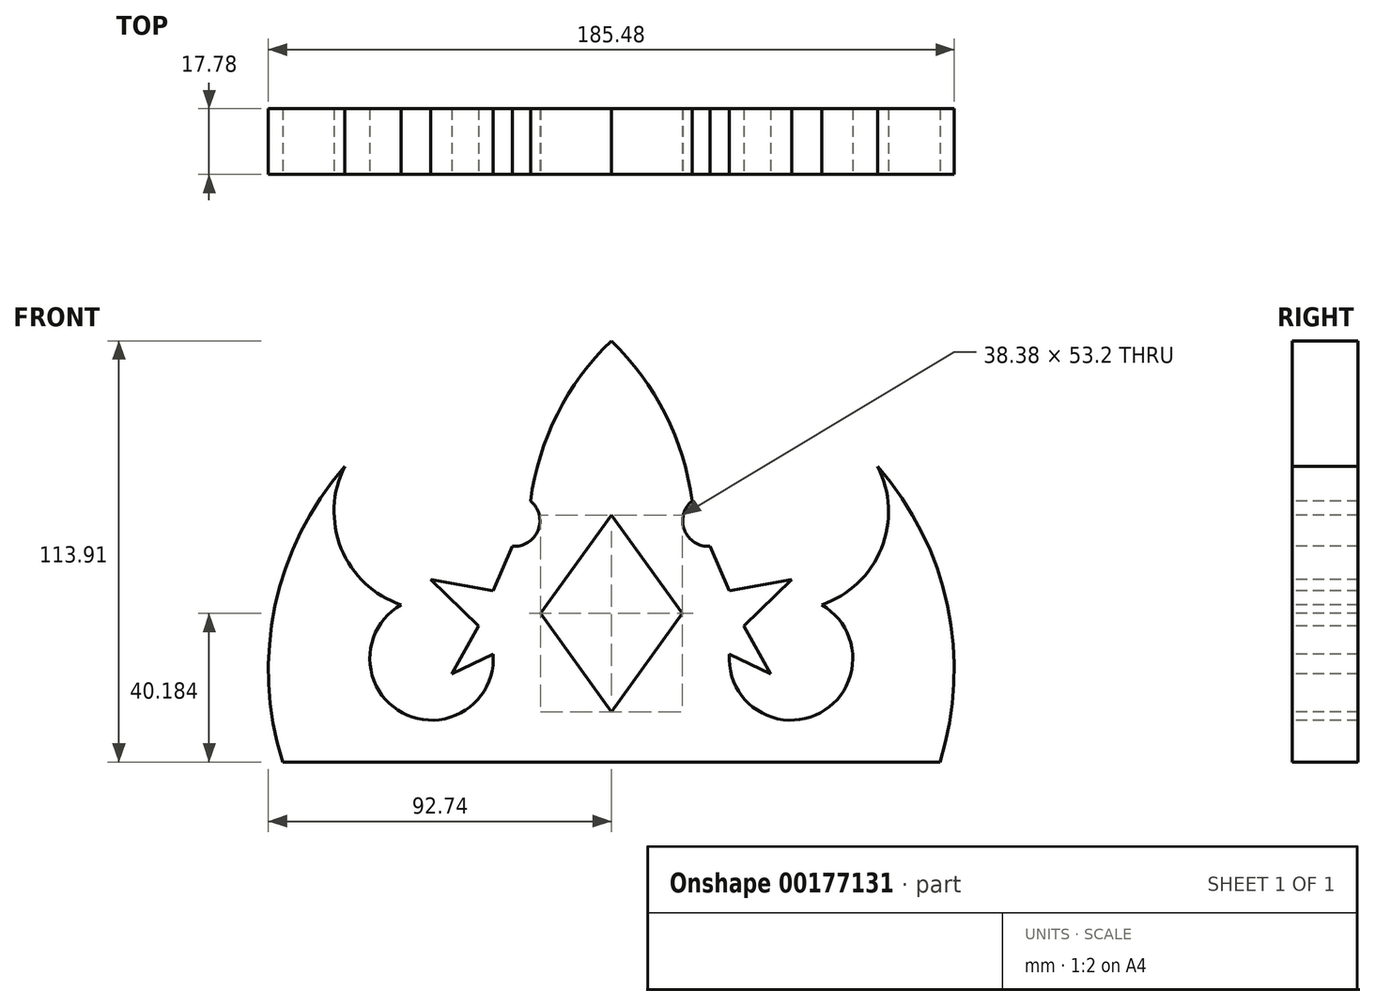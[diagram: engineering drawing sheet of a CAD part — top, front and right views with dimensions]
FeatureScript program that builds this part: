
annotation { "Feature Type Name" : "Feature", "Feature Type Description" : "" }
export const myFeature = defineFeature(function(context is Context, id is Id, definition is map)
    precondition{}
    {
        {
            var Q0;
            Q0=qCreatedBy(makeId("Front.planeOp"),FACE);
            var sketch = newSketch(context, id + "F0", { "sketchPlane" : qUnion([Q0])});
            skLineSegment(sketch, "E0", {"start": v(0, 0) * mm, "end": v(88.9, 0) * mm});
            skLineSegment(sketch, "E1", {"start": v(0, 0) * mm, "end": v(-88.9, 0) * mm});
            skArc(sketch, "E2", {"start": v(-72.07, 79.92) * mm, "mid": v(-90.96, 42.16) * mm, "end": v(-88.9, 0) * mm});
            skArc(sketch, "E3", {"start": v(-72.07, 79.92) * mm, "mid": v(-73.05, 57.73) * mm, "end": v(-56.9, 42.5) * mm});
            skArc(sketch, "E4", {"start": v(-56.9, 42.5) * mm, "mid": v(-56.5, 13.27) * mm, "end": v(-31.93, 29.1) * mm});
            skLineSegment(sketch, "E5", {"start": v(-31.93, 29.1) * mm, "end": v(-43.12, 23.84) * mm});
            skLineSegment(sketch, "E6", {"start": v(-43.12, 23.84) * mm, "end": v(-35.9, 36.76) * mm});
            skLineSegment(sketch, "E7", {"start": v(-35.9, 36.76) * mm, "end": v(-48.82, 49.3) * mm});
            skLineSegment(sketch, "E8", {"start": v(-48.82, 49.3) * mm, "end": v(-31.93, 46.26) * mm});
            skLineSegment(sketch, "E9", {"start": v(-31.93, 46.26) * mm, "end": v(-26.76, 58.33) * mm});
            skLineSegment(sketch, "E10", {"start": v(0, 66.79) * mm, "end": v(-19.2, 40.2) * mm});
            skLineSegment(sketch, "E11", {"start": v(-19.2, 40.2) * mm, "end": v(0, 13.58) * mm});
            skArc(sketch, "E12", {"start": v(-26.76, 58.33) * mm, "mid": v(-19.8, 62.66) * mm, "end": v(-21.83, 70.59) * mm});
            skArc(sketch, "E13", {"start": v(0, 113.9) * mm, "mid": v(-14.6, 94.1) * mm, "end": v(-21.83, 70.59) * mm});
            skArc(sketch, "E14.MirrorCS", {"start": v(56.9, 42.5) * mm, "mid": v(56.5, 13.27) * mm, "end": v(31.93, 29.1) * mm});
            skLineSegment(sketch, "E15.MirrorCS", {"start": v(19.2, 40.2) * mm, "end": v(0, 13.58) * mm});
            skLineSegment(sketch, "E16.MirrorCS", {"start": v(0, 66.79) * mm, "end": v(19.2, 40.2) * mm});
            skArc(sketch, "E17.MirrorCS", {"start": v(0, 113.9) * mm, "mid": v(14.6, 94.1) * mm, "end": v(21.83, 70.59) * mm});
            skArc(sketch, "E18.MirrorCS", {"start": v(26.76, 58.33) * mm, "mid": v(19.8, 62.66) * mm, "end": v(21.83, 70.59) * mm});
            skLineSegment(sketch, "E19.MirrorCS", {"start": v(31.93, 46.26) * mm, "end": v(26.76, 58.33) * mm});
            skLineSegment(sketch, "E20.MirrorCS", {"start": v(48.82, 49.3) * mm, "end": v(31.93, 46.26) * mm});
            skLineSegment(sketch, "E21.MirrorCS", {"start": v(35.9, 36.76) * mm, "end": v(48.82, 49.3) * mm});
            skLineSegment(sketch, "E22.MirrorCS", {"start": v(43.12, 23.84) * mm, "end": v(35.9, 36.76) * mm});
            skLineSegment(sketch, "E23.MirrorCS", {"start": v(31.93, 29.1) * mm, "end": v(43.12, 23.84) * mm});
            skArc(sketch, "E24.MirrorCS", {"start": v(72.07, 79.92) * mm, "mid": v(73.05, 57.73) * mm, "end": v(56.9, 42.5) * mm});
            skArc(sketch, "E25.MirrorCS", {"start": v(72.07, 79.92) * mm, "mid": v(90.96, 42.16) * mm, "end": v(88.9, 0) * mm});
            skSolve(sketch);
        }
        {
            var Q0;
            Q0=makeQuery(id+"F0.imprint","IMPRINT",FACE,{"disambiguationData":[TD([[makeQuery(id+"F0.imprint","IMPRINT",EDGE,{"derivedFrom":sQuery(id+"F0.wireOp",EDGE,"E0")}),1.0]])]});
            extrude(context, id + "F1", {"entities" : qUnion([Q0]), "oppositeDirection" : true, "depth" : 17.78 * mm});
        }
    });
